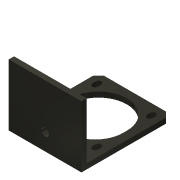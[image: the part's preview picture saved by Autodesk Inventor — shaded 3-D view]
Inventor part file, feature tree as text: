
AUTODESK INVENTOR PART (.ipt)
format: ipt  version: 2014 (Build 180170000, 170)  size: 140,800 bytes
history: native  units: mm
features: extrude x2, sketch x2, chamfer x1
ambient origin geometry x8: Origin, YZ Plane, XZ Plane, XY Plane, X Axis, Y Axis, Z Axis, Center Point
bodies: Solid1 (feature_tree)
feature tree (5):
  extrude  "Extrusion1"  Depth=41.3mm
  extrude  "Extrusion2"  Depth=3.0mm
  chamfer  "Chamfer1"  Distance=16.0mm
  sketch  "Sketch1"  dims[d0=51.0mm d1=41.3mm]
  sketch  "Sketch2"  dims[d2=28.4mm d3=2.0mm d4=16.0mm d5=2.0mm d6=31.0mm d7=31.0mm d8=1.6mm d10=15.5mm d11=15.5mm d12=3.0mm d13=0.0mm d14=35.0mm d15=9.5mm d16=4.3mm d17=3.0mm d18=0.0mm d19=3.0mm d20=2.0mm d21=45.0deg]
